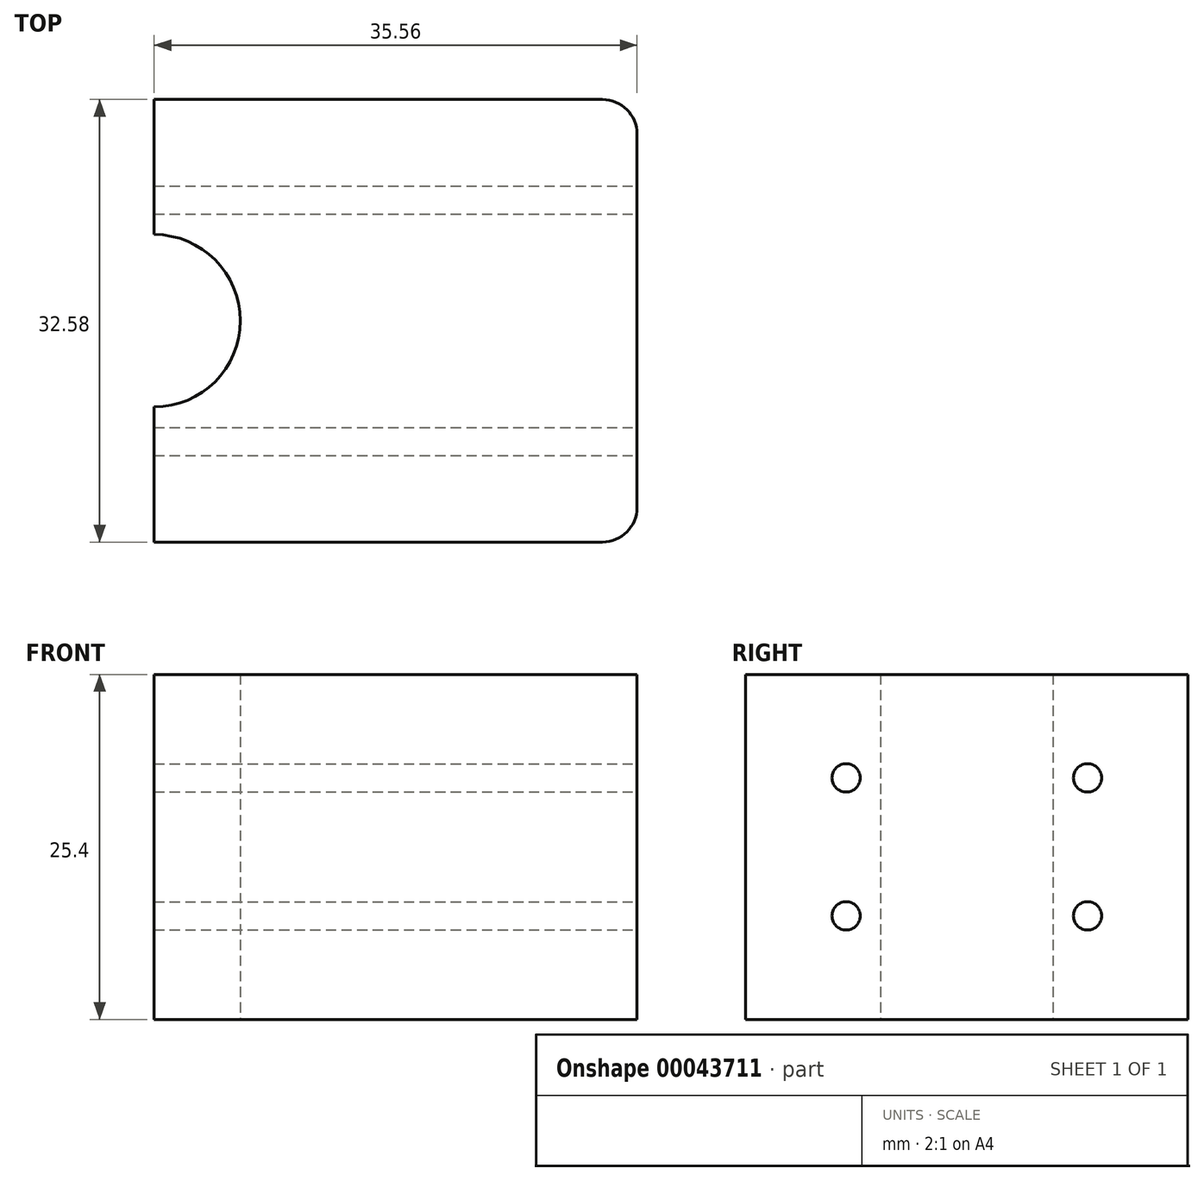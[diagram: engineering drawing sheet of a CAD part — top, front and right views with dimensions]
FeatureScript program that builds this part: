
annotation { "Feature Type Name" : "Feature", "Feature Type Description" : "" }
export const myFeature = defineFeature(function(context is Context, id is Id, definition is map)
    precondition{}
    {
        {
            var Q0;
            Q0=qCreatedBy(makeId("Top.planeOp"),FACE);
            var sketch = newSketch(context, id + "F0", { "sketchPlane" : qUnion([Q0])});
            skLineSegment(sketch, "E0.rect.bottom", {"start": v(-17.78, -16.3) * mm, "end": v(15.24, -16.3) * mm});
            skLineSegment(sketch, "E0.rect.top", {"start": v(-17.78, 16.3) * mm, "end": v(15.24, 16.3) * mm});
            skLineSegment(sketch, "E0.rect.left", {"start": v(-17.78, -16.3) * mm, "end": v(-17.78, -6.35) * mm});
            skLineSegment(sketch, "E0.rect.right", {"start": v(17.78, -13.75) * mm, "end": v(17.78, 13.75) * mm});
            skPoint(sketch, "E0.rect.middle", {"position": v(0, 0) * mm});
            skLineSegment(sketch, "E1", {"start": v(-17.78, 0) * mm, "end": v(17.78, 0) * mm, "construction": true});
            skArc(sketch, "E2", {"start": v(-17.78, -6.35) * mm, "mid": v(-11.43, 0) * mm, "end": v(-17.78, 6.35) * mm});
            skPoint(sketch, "E3.visualSharp", {"position": v(17.78, 16.3) * mm});
            skArc(sketch, "E3.filletArc", {"start": v(17.78, 13.75) * mm, "mid": v(17.04, 15.55) * mm, "end": v(15.24, 16.3) * mm});
            skPoint(sketch, "E4.visualSharp", {"position": v(17.78, -16.3) * mm});
            skArc(sketch, "E4.filletArc", {"start": v(15.24, -16.3) * mm, "mid": v(17.04, -15.55) * mm, "end": v(17.78, -13.75) * mm});
            skLineSegment(sketch, "E5.trimOffspring", {"start": v(-17.78, 6.35) * mm, "end": v(-17.78, 16.3) * mm});
            skSolve(sketch);
        }
        {
            var Q0;
            Q0=makeQuery(id+"F0.imprint","IMPRINT",FACE,{"disambiguationData":[TD([[makeQuery(id+"F0.imprint","IMPRINT",EDGE,{"derivedFrom":sQuery(id+"F0.wireOp",EDGE,"E0.rect.bottom")}),1.0]])]});
            extrude(context, id + "F1", {"entities" : qUnion([Q0]), "depth" : 25.4 * mm});
        }
        {
            var Q0;
            Q0=makeQuery(id+"F1.opExtrude","SWEPT_FACE",FACE,{"disambiguationData":[OSD([sQuery(id+"F0.wireOp",EDGE,"E0.rect.right")])]});
            var sketch = newSketch(context, id + "F2", { "sketchPlane" : qUnion([Q0])});
            skLineSegment(sketch, "E6", {"start": v(0, 25.4) * mm, "end": v(0, 0) * mm, "construction": true});
            skLineSegment(sketch, "E7", {"start": v(-13.75, 12.7) * mm, "end": v(13.75, 12.7) * mm, "construction": true});
            skCircle(sketch, "E8", {"center": v(-8.89, 17.78) * mm, "radius": 1.04 * mm});
            skCircle(sketch, "E9.MirrorC", {"center": v(8.9, 17.78) * mm, "radius": 1.04 * mm});
            skCircle(sketch, "E10.MirrorC", {"center": v(-8.89, 7.62) * mm, "radius": 1.04 * mm});
            skCircle(sketch, "E11.MirrorC", {"center": v(8.9, 7.62) * mm, "radius": 1.04 * mm});
            skSolve(sketch);
        }
        {
            var Q0;
            Q0=sQuery(id+"F2.wireOp",VERTEX,"9sQDPwwv-kVNf-PWTK-zYvr-nysep9C1BNDA.start");
            var Q1;
            Q1=sQuery(id+"F2.wireOp",VERTEX,"ecbdfbf2-897d-45c3-8258-0ca4c12224a3.center");
            var Q2;
            Q2=sQuery(id+"F2.wireOp",VERTEX,"wmfYGqAr-oXZi-TUJR-SepK-T9XxWOzFN1r8.start");
            var Q3;
            Q3=sQuery(id+"F2.wireOp",VERTEX,"570e05f1-ed43-4619-a79c-27951dcda8b0.center");
            var Q4;
            Q4=sQuery(id+"F2.wireOp",VERTEX,"E8.center");
            var Q5;
            Q5=sQuery(id+"F2.wireOp",VERTEX,"E10.MirrorC.center");
            var Q6;
            Q6=sQuery(id+"F2.wireOp",VERTEX,"E9.MirrorC.center");
            var Q7;
            Q7=sQuery(id+"F2.wireOp",VERTEX,"E11.MirrorC.center");
            var Q8;
            Q8=makeQuery(id+"F1.opExtrude","SWEPT_BODY",BODY,{"disambiguationData":[OSD([sQuery(id+"F0.wireOp",EDGE,"E0.rect.bottom"),sQuery(id+"F0.wireOp",EDGE,"E0.rect.top"),sQuery(id+"F0.wireOp",EDGE,"E0.rect.left"),sQuery(id+"F0.wireOp",EDGE,"E0.rect.right"),sQuery(id+"F0.wireOp",EDGE,"E2"),sQuery(id+"F0.wireOp",EDGE,"E3.filletArc"),sQuery(id+"F0.wireOp",EDGE,"E4.filletArc"),sQuery(id+"F0.wireOp",EDGE,"E5.trimOffspring")])]});
            hole(context, id + "F3", {"style" : HoleStyle.SIMPLE, "holeDiameter" : 2.08 * mm, "endStyle" : HoleEndStyle.THROUGH, "locations" : qUnion([Q0, Q1, Q2, Q3, Q4, Q5, Q6, Q7]), "scope" : qUnion([Q8])});
        }
    });
